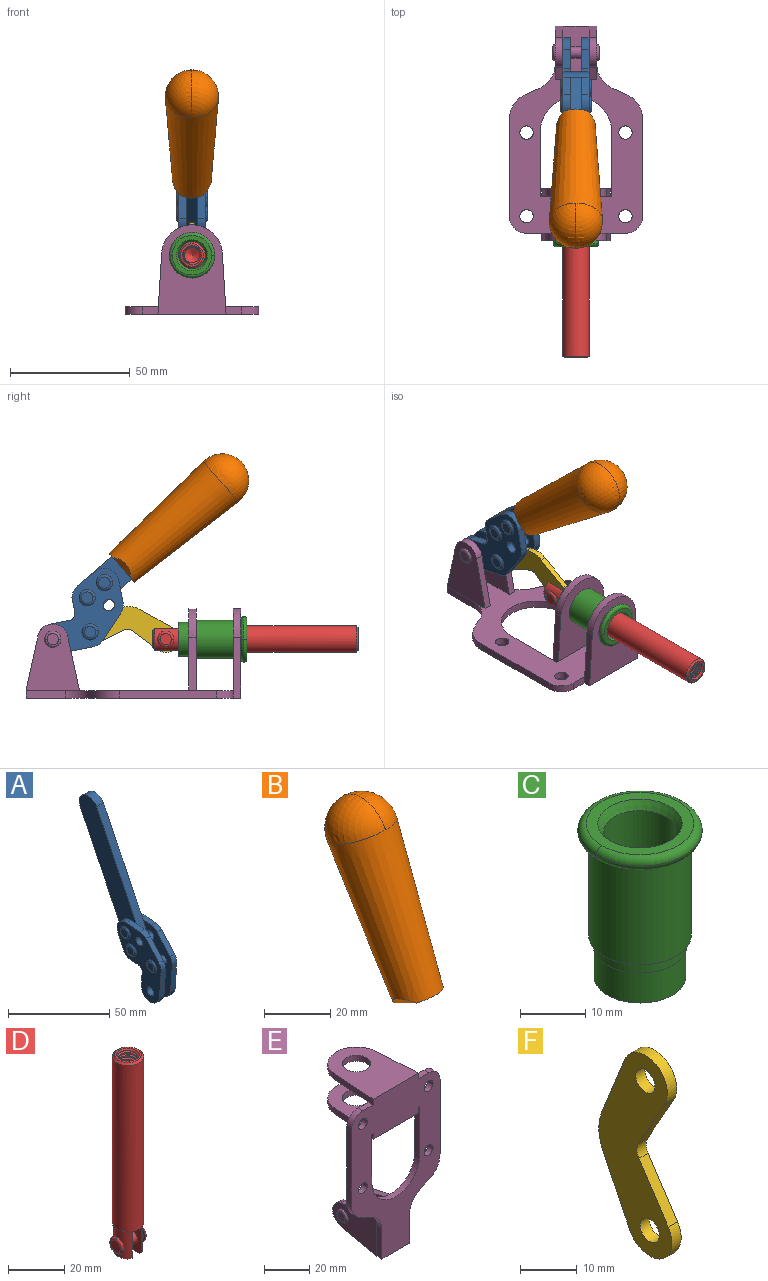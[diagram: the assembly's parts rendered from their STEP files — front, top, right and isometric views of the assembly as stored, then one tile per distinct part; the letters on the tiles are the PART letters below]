
ASSEMBLY  parts=6 mates=7
PART A: 59 faces, bbox 12.9x60.2x99.6 mm
  f0: torus R=2.39mm, axis (-1,0,0), area 14.9mm2, adj f20,f43,f51
  f1: torus R=2.39mm, axis (-1,0,0), area 14.9mm2, adj f19,f42,f51
  f2: torus R=2.39mm, axis (-1,0,0), area 14.9mm2, adj f18,f35,f51
  f3: torus R=2.39mm, axis (-1,0,0), area 14.9mm2, adj f14,f17,f23
  f4: torus R=2.39mm, axis (-1,0,0), area 14.9mm2, adj f13,f16,f23
  f5: torus R=2.39mm, axis (-1,0,0), area 14.9mm2, adj f12,f15,f23
  f6: cylinder r=2.39mm len=4.78mm, axis (1,0,0), area 46.5mm2, adj f48,f50,f51
  f7: cylinder r=2.39mm len=4.78mm, axis (1,0,0), area 46.5mm2, adj f50,f51
  f8: cylinder r=6.35mm len=12.68mm, axis (1,0,0), area 61.8mm2, adj f38,f39,f50,f51
  f9: cylinder r=2.39mm len=4.78mm, axis (-1,0,0), area 70.5mm2, adj f46,f50
  f10: cylinder r=2.39mm len=4.78mm, axis (-1,0,0), area 46.5mm2, adj f23,f45,f46
  f11: cylinder r=2.39mm len=4.78mm, axis (-1,0,0), area 46.5mm2, adj f23,f46
  f12: plane 4.78x4.78mm, normal (1,0,0), area 17.9mm2, adj f5,f15
  f13: plane 4.78x4.78mm, normal (1,0,0), area 17.9mm2, adj f4,f16
  f14: plane 4.78x4.78mm, normal (1,0,0), area 17.9mm2, adj f3,f17
  f15: torus R=2.39mm, axis (-1,0,0), area 14.9mm2, adj f5,f12,f23
  f16: torus R=2.39mm, axis (-1,0,0), area 14.9mm2, adj f4,f13,f23
  f17: torus R=2.39mm, axis (-1,0,0), area 14.9mm2, adj f3,f14,f23
  f18: plane 4.78x4.78mm, normal (-1,0,0), area 17.9mm2, adj f2,f35
  f19: plane 4.78x4.78mm, normal (-1,0,0), area 17.9mm2, adj f1,f42
  f20: plane 4.78x4.78mm, normal (-1,0,0), area 17.9mm2, adj f0,f43
  f21: plane 2.26x0.2mm, normal (1,0,0), area 0.2mm2, adj f31,f44
  f22: plane 2.26x0.2mm, normal (-1,0,0), area 0.2mm2, adj f41,f44
  f23: plane 39.37x30.77mm, normal (1,0,0), area 565.5mm2, adj f3,f4,f5,f10,f11,f15,f16,f17
  f24: cylinder r=6.1mm len=4.15mm, axis (-1,0,0), area 14.7mm2, adj f23,f25,f32,f46
  f25: plane 10.25x9.01mm, normal (0,-0.75,0.66), area 42.3mm2, adj f23,f24,f26,f46
  f26: cylinder r=6.35mm len=4.64mm, axis (-1,0,0), area 15.6mm2, adj f23,f25,f27,f46
  f27: plane 15.84x3.1mm, normal (0,-1,-0.07), area 49.2mm2, adj f23,f26,f28,f46
  f28: cylinder r=6.35mm len=12.68mm, axis (-1,0,0), area 61.8mm2, adj f23,f27,f29,f46
  f29: plane 8.11x3.1mm, normal (0,1,0.07), area 25.2mm2, adj f23,f28,f30,f46
  f30: cylinder r=3.05mm len=3.25mm, axis (-1,0,0), area 14.8mm2, adj f23,f29,f31,f46
  f31: plane 5.99x3.1mm, normal (0,0.07,-1), area 18.6mm2, adj f21,f23,f30,f44,f46
  f32: plane 9.5x3.1mm, normal (0,-0.07,1), area 29.5mm2, adj f23,f24,f33,f46,f47
  f33: cylinder r=6.1mm len=8.63mm, axis (-1,0,0), area 39.1mm2, adj f23,f32,f34,f47
  f34: plane 8.65x3.96mm, normal (0,0.91,-0.42), area 29.5mm2, adj f23,f33,f44,f47
  f35: torus R=2.39mm, axis (-1,0,0), area 14.9mm2, adj f2,f18,f51
  f36: plane 10.25x9.01mm, normal (0,-0.75,0.66), area 42.3mm2, adj f37,f49,f50,f51
  f37: cylinder r=6.35mm len=4.64mm, axis (1,0,0), area 15.6mm2, adj f36,f38,f50,f51
  f38: plane 15.84x3.1mm, normal (0,-1,-0.07), area 49.2mm2, adj f8,f37,f50,f51
  f39: plane 8.11x3.1mm, normal (0,1,0.07), area 25.2mm2, adj f8,f40,f50,f51
  f40: cylinder r=3.05mm len=3.25mm, axis (1,0,0), area 14.8mm2, adj f39,f41,f50,f51
  f41: plane 5.99x3.1mm, normal (0,0.07,-1), area 18.6mm2, adj f22,f40,f44,f50,f51
  f42: torus R=2.39mm, axis (-1,0,0), area 14.9mm2, adj f1,f19,f51
  f43: torus R=2.39mm, axis (-1,0,0), area 14.9mm2, adj f0,f20,f51
  f44: cylinder r=6.35mm len=12.12mm, axis (-1,0,0), area 128.9mm2, adj f21,f22,f23,f31,f34,f41,f46,f47
  f45: plane 2.65x1.35mm, normal (1,0,0), area 1mm2, adj f10,f55
  f46: plane 39.08x20.42mm, normal (-1,0,0), area 412.5mm2, adj f9,f10,f11,f24,f25,f26,f27,f28
  f47: plane 77.62x39.82mm, normal (1,0,0), area 850mm2, adj f32,f33,f34,f44,f53,f54,f55
  f48: plane 2.65x1.35mm, normal (-1,0,0), area 1mm2, adj f6,f55
  f49: cylinder r=6.1mm len=4.15mm, axis (1,0,0), area 14.7mm2, adj f36,f50,f51,f56
  f50: plane 39.08x20.42mm, normal (1,0,0), area 412.5mm2, adj f6,f7,f8,f9,f36,f37,f38,f39
  f51: plane 39.37x30.77mm, normal (-1,0,0), area 565.5mm2, adj f0,f1,f2,f6,f7,f8,f35,f36
  f52: plane 8.65x3.96mm, normal (0,0.91,-0.42), area 29.5mm2, adj f44,f51,f57,f58
  f53: plane 68.49x33.4mm, normal (0,0.9,-0.44), area 358.1mm2, adj f44,f47,f54,f58
  f54: cylinder r=6.35mm len=12.06mm, axis (1,0,0), area 93.7mm2, adj f47,f53,f55,f58
  f55: plane 68.49x33.4mm, normal (0,-0.9,0.44), area 358.1mm2, adj f44,f45,f46,f47,f48,f50,f54,f58
  f56: plane 9.5x3.1mm, normal (0,-0.07,1), area 29.5mm2, adj f49,f50,f51,f57,f58
  f57: cylinder r=6.1mm len=8.63mm, axis (1,0,0), area 39.1mm2, adj f51,f52,f56,f58
  f58: plane 77.62x39.82mm, normal (-1,0,0), area 850mm2, adj f44,f52,f53,f54,f55,f56,f57
PART B: 11 faces, bbox 22.3x42.6x64.5 mm
  f0: sphere r=11.13mm, area 411.4mm2, adj f1,f8
  f1: cone r=11.11mm half-angle=3.3deg, axis (0,0.44,0.9), area 3251.8mm2, adj f0,f7,f8,f9,f10
  f2: cylinder r=6.16mm len=11.7mm, axis (1,0,0), area 89.5mm2, adj f3,f4,f5,f6
  f3: plane 60.23x36.75mm, normal (-1,0,0), area 763.6mm2, adj f2,f4,f6,f10
  f4: plane 51.37x25.05mm, normal (0,0.9,-0.44), area 264.2mm2, adj f2,f3,f5,f10
  f5: plane 60.23x36.75mm, normal (1,0,0), area 763.6mm2, adj f2,f4,f6,f10
  f6: plane 51.37x25.05mm, normal (0,-0.9,0.44), area 264.2mm2, adj f2,f3,f5,f10
  f7: plane 9.95x5.95mm, normal (0.71,-0.31,-0.64), area 25.8mm2, adj f1,f10
  f8: sphere r=11.13mm, area 411.4mm2, adj f0,f1
  f9: plane 9.95x5.95mm, normal (-0.71,-0.31,-0.64), area 25.8mm2, adj f1,f10
  f10: plane 14.27x11.38mm, normal (0,-0.44,-0.9), area 106.7mm2, adj f1,f3,f4,f5,f6,f7,f9
PART C: 15 faces, bbox 20.6x20.6x28.7 mm
  f0: torus R=8.26mm, axis (0,0,1), area 56.8mm2, adj f1,f10,f12
  f1: torus R=8.26mm, axis (0,0,1), area 56.8mm2, adj f0,f6,f13
  f2: cylinder r=5.59mm len=25.91mm, axis (0,0,1), area 909.6mm2, adj f3,f4
  f3: cone r=6.86mm half-angle=45deg, axis (0,0,-1), area 70.2mm2, adj f2,f14
  f4: cone r=6.47mm half-angle=30deg, axis (0,0,1), area 66.7mm2, adj f2,f13
  f5: cylinder r=7.04mm len=14.07mm, axis (0,0,1), area 252.6mm2, adj f11,f14
  f6: torus R=8.26mm, axis (0,0,1), area 56.8mm2, adj f1,f12,f13
  f7: cylinder r=7.16mm len=14.33mm, axis (0,0,1), area 91.5mm2, adj f9,f11
  f8: cylinder r=7.86mm len=18.42mm, axis (0,0,1), area 909.6mm2, adj f9,f10
  f9: plane 15.72x15.72mm, normal (0,0,-1), area 33mm2, adj f7,f8
  f10: plane 16.51x16.51mm, normal (0,0,-1), area 19.9mm2, adj f0,f8,f12
  f11: plane 14.33x14.33mm, normal (0,0,-1), area 5.7mm2, adj f5,f7
  f12: torus R=8.26mm, axis (0,0,1), area 56.8mm2, adj f0,f6,f10
  f13: plane 16.51x16.51mm, normal (0,0,1), area 82.7mm2, adj f1,f4,f6
  f14: plane 14.07x14.07mm, normal (0,0,-1), area 7.8mm2, adj f3,f5
PART D: 48 faces, bbox 12.6x11.1x86.1 mm
  f0: torus R=2.41mm, axis (-1,0,0), area 15mm2, adj f30,f32,f34
  f1: torus R=2.41mm, axis (-1,0,0), area 15mm2, adj f29,f31,f33
  f2: cylinder r=5.54mm len=72.39mm, axis (0,0,1), area 2518.5mm2, adj f3,f4,f42,f43
  f3: cone r=5.54mm half-angle=45deg, axis (0,0,1), area 7.6mm2, adj f2,f5,f41
  f4: cone r=5.54mm half-angle=45deg, axis (0,0,-1), area 34.9mm2, adj f2,f39
  f5: cylinder r=5.08mm len=11.48mm, axis (0,0,1), area 108.3mm2, adj f3,f7,f8,f41
  f6: cylinder r=2.41mm len=4.83mm, axis (-1,0,0), area 71.2mm2, adj f40,f41
  f7: cylinder r=2.41mm len=4.83mm, axis (-1,0,0), area 7.6mm2, adj f5,f34
  f8: cone r=5.08mm half-angle=45deg, axis (0,0,1), area 10.6mm2, adj f5,f37,f41
  f9: cone r=3.98mm half-angle=45deg, axis (0,0,1), area 17.6mm2, adj f27,f39,f45,f46,f47
  f10: cylinder r=2.41mm len=4.83mm, axis (-1,0,0), area 7.6mm2, adj f33,f38
  f11: cylinder r=3.2mm len=6.4mm, axis (0,0,1), area 78.4mm2, adj f12,f28,f44,f45,f47
  f12: cylinder r=3.2mm len=6.4mm, axis (0,0,1), area 10.5mm2, adj f11,f13,f45,f47
  f13: cylinder r=3.2mm len=6.4mm, axis (0,0,1), area 10.5mm2, adj f12,f14,f45,f47
  f14: cylinder r=3.2mm len=6.4mm, axis (0,0,1), area 10.5mm2, adj f13,f15,f45,f47
  f15: cylinder r=3.2mm len=6.4mm, axis (0,0,1), area 10.5mm2, adj f14,f16,f45,f47
  f16: cylinder r=3.2mm len=6.4mm, axis (0,0,1), area 10.5mm2, adj f15,f17,f45,f47
  f17: cylinder r=3.2mm len=6.4mm, axis (0,0,1), area 10.5mm2, adj f16,f18,f45,f47
  f18: cylinder r=3.2mm len=6.4mm, axis (0,0,1), area 10.5mm2, adj f17,f19,f45,f47
  f19: cylinder r=3.2mm len=6.4mm, axis (0,0,1), area 10.5mm2, adj f18,f20,f45,f47
  f20: cylinder r=3.2mm len=6.4mm, axis (0,0,1), area 10.5mm2, adj f19,f21,f45,f47
  f21: cylinder r=3.2mm len=6.4mm, axis (0,0,1), area 10.5mm2, adj f20,f22,f45,f47
  f22: cylinder r=3.2mm len=6.4mm, axis (0,0,1), area 10.5mm2, adj f21,f23,f45,f47
  f23: cylinder r=3.2mm len=6.4mm, axis (0,0,1), area 10.5mm2, adj f22,f24,f45,f47
  f24: cylinder r=3.2mm len=6.4mm, axis (0,0,1), area 10.5mm2, adj f23,f25,f45,f47
  f25: cylinder r=3.2mm len=6.4mm, axis (0,0,1), area 10.5mm2, adj f24,f26,f45,f47
  f26: cylinder r=3.2mm len=6.4mm, axis (0,0,1), area 10.5mm2, adj f25,f27,f45,f47
  f27: cylinder r=3.2mm len=6.4mm, axis (0,0,1), area 7.4mm2, adj f9,f26,f45,f47
  f28: cone r=3.2mm half-angle=60deg, axis (0,0,1), area 37.2mm2, adj f11
  f29: plane 4.83x4.83mm, normal (-1,0,0), area 18.3mm2, adj f1,f31
  f30: plane 4.83x4.83mm, normal (1,0,0), area 18.3mm2, adj f0,f32
  f31: torus R=2.41mm, axis (-1,0,0), area 15mm2, adj f1,f29,f33
  f32: torus R=2.41mm, axis (-1,0,0), area 15mm2, adj f0,f30,f34
  f33: plane 6.83x6.83mm, normal (1,0,0), area 18.3mm2, adj f1,f10,f31
  f34: plane 6.83x6.83mm, normal (-1,0,0), area 18.3mm2, adj f0,f7,f32
  f35: cone r=5.08mm half-angle=45deg, axis (0,0,1), area 10.6mm2, adj f36,f38,f40
  f36: plane 7.25x1.97mm, normal (0,0,-1), area 10mm2, adj f35,f40
  f37: plane 7.25x1.97mm, normal (0,0,-1), area 10mm2, adj f8,f41
  f38: cylinder r=5.08mm len=11.48mm, axis (0,0,1), area 108.3mm2, adj f10,f35,f40,f42
  f39: plane 9.55x9.55mm, normal (0,0,1), area 22mm2, adj f4,f9
  f40: plane 12.76x10.09mm, normal (1,0,0), area 95.7mm2, adj f6,f35,f36,f38,f42,f43
  f41: plane 12.76x10.09mm, normal (-1,0,0), area 95.7mm2, adj f3,f5,f6,f8,f37,f43
  f42: cone r=5.54mm half-angle=45deg, axis (0,0,1), area 7.6mm2, adj f2,f38,f40
  f43: plane 11.07x4.7mm, normal (0,0,-1), area 50.4mm2, adj f2,f40,f41
  f44: plane 0.89x0.62mm, normal (-1,0,0), area 0.3mm2, adj f11,f45,f46,f47
  f45: bspline ~24.8x7.63mm, area 266.6mm2, adj f9,f11,f12,f13,f14,f15,f16,f17
  f46: bspline ~24.87x7.63mm, area 73.6mm2, adj f9,f44,f45,f47
  f47: bspline ~24.98x7.63mm, area 272.5mm2, adj f9,f11,f12,f13,f14,f15,f16,f17
PART E: 55 faces, bbox 55.7x37.4x89.8 mm
  f0: torus R=2.41mm, axis (-1,0,0), area 15mm2, adj f11,f15,f25
  f1: torus R=2.41mm, axis (-1,0,0), area 15mm2, adj f10,f12,f22
  f2: cylinder r=2.78mm len=5.56mm, axis (0,-1,0), area 54.2mm2, adj f30,f54
  f3: cylinder r=14.99mm len=29.97mm, axis (0,-1,0), area 145.9mm2, adj f30,f49,f53,f54
  f4: cylinder r=2.78mm len=5.56mm, axis (0,-1,0), area 54.2mm2, adj f30,f54
  f5: cylinder r=2.78mm len=5.56mm, axis (0,-1,0), area 54.2mm2, adj f30,f54
  f6: cylinder r=2.78mm len=5.56mm, axis (0,-1,0), area 54.2mm2, adj f30,f54
  f7: cylinder r=6.35mm len=12.7mm, axis (0,0,1), area 123.6mm2, adj f27,f51
  f8: cylinder r=6.35mm len=12.7mm, axis (0,0,-1), area 124.7mm2, adj f21,f35
  f9: cylinder r=2.41mm len=11.18mm, axis (-1,0,0), area 169.4mm2, adj f16,f19
  f10: plane 4.83x4.83mm, normal (1,0,0), area 18.3mm2, adj f1,f12
  f11: plane 4.83x4.83mm, normal (-1,0,0), area 18.3mm2, adj f0,f15
  f12: torus R=2.41mm, axis (-1,0,0), area 15mm2, adj f1,f10,f22
  f13: cylinder r=6.35mm len=12.41mm, axis (1,0,0), area 53.4mm2, adj f18,f19,f22,f23
  f14: cylinder r=6.35mm len=12.41mm, axis (-1,0,0), area 53.4mm2, adj f16,f17,f24,f25
  f15: torus R=2.41mm, axis (-1,0,0), area 15mm2, adj f0,f11,f25
  f16: plane 27.86x22.35mm, normal (1,0,0), area 425.4mm2, adj f9,f14,f17,f24,f30
  f17: plane 22.86x4.97mm, normal (0,0.21,0.98), area 72.5mm2, adj f14,f16,f25,f30
  f18: plane 22.86x4.97mm, normal (0,0.21,0.98), area 72.5mm2, adj f13,f19,f22,f30
  f19: plane 27.86x22.35mm, normal (-1,0,0), area 425.4mm2, adj f9,f13,f18,f23,f30
  f20: cylinder r=12.7mm len=25.35mm, axis (0,0,-1), area 119.8mm2, adj f21,f34,f35,f36
  f21: plane 34.21x28.07mm, normal (0,0,-1), area 702.4mm2, adj f8,f20,f30,f34,f36
  f22: plane 27.96x22.45mm, normal (1,0,0), area 407.2mm2, adj f1,f12,f13,f18,f23,f30,f42,f43
  f23: plane 22.86x4.97mm, normal (0,0.21,-0.98), area 72.5mm2, adj f13,f19,f22,f44
  f24: plane 22.86x4.97mm, normal (0,0.21,-0.98), area 72.5mm2, adj f14,f16,f25,f44
  f25: plane 27.86x22.35mm, normal (-1,0,0), area 407.1mm2, adj f0,f14,f15,f17,f24,f30,f45,f46
  f26: plane 3.1x0.95mm, normal (0,0,-1), area 2.7mm2, adj f30,f49,f50,f54
  f27: plane 34.21x28.07mm, normal (0,0,1), area 702.4mm2, adj f7,f28,f30,f50,f52
  f28: cylinder r=12.7mm len=25.35mm, axis (0,0,1), area 118.8mm2, adj f27,f50,f51,f52
  f29: plane 3.1x0.95mm, normal (0,0,-1), area 2.7mm2, adj f30,f52,f53,f54
  f30: plane 86.54x55.63mm, normal (0,1,0), area 2362.9mm2, adj f2,f3,f4,f5,f6,f16,f17,f18
  f31: plane 40.56x3.1mm, normal (-1,0,0), area 125.7mm2, adj f30,f32,f48,f54
  f32: cylinder r=7.11mm len=7.11mm, axis (0,-1,0), area 34.6mm2, adj f30,f31,f33,f54
  f33: plane 6.67x3.1mm, normal (0,0,1), area 20.4mm2, adj f30,f32,f34,f54
  f34: plane 25.39x3.13mm, normal (-1,0.06,0), area 79.5mm2, adj f20,f21,f33,f35,f54
  f35: plane 37.31x28.45mm, normal (0,0,1), area 789.9mm2, adj f8,f20,f34,f36,f54
  f36: plane 25.39x3.13mm, normal (1,0.06,0), area 79.5mm2, adj f20,f21,f35,f37,f54
  f37: plane 6.67x3.1mm, normal (0,0,1), area 20.4mm2, adj f30,f36,f38,f54
  f38: cylinder r=7.11mm len=7.11mm, axis (0,-1,0), area 34.6mm2, adj f30,f37,f39,f54
  f39: plane 40.56x3.1mm, normal (1,0,0), area 125.7mm2, adj f30,f38,f40,f54
  f40: cylinder r=11.18mm len=10.16mm, axis (0,-1,0), area 39.5mm2, adj f30,f39,f41,f54
  f41: plane 6.09x3.1mm, normal (0.42,0,-0.91), area 20.8mm2, adj f30,f40,f42,f54
  f42: cylinder r=11.18mm len=9.41mm, axis (0,-1,0), area 37.2mm2, adj f22,f30,f41,f43,f54
  f43: plane 16.5x3.1mm, normal (1,0,0), area 51.1mm2, adj f22,f42,f44,f54
  f44: plane 17.37x3.1mm, normal (0,0,-1), area 53.8mm2, adj f23,f24,f30,f43,f45,f54
  f45: plane 16.5x3.1mm, normal (-1,0,0), area 51.1mm2, adj f25,f44,f46,f54
  f46: cylinder r=11.18mm len=9.41mm, axis (0,-1,0), area 37.2mm2, adj f25,f30,f45,f47,f54
  f47: plane 6.09x3.1mm, normal (-0.42,0,-0.91), area 20.8mm2, adj f30,f46,f48,f54
  f48: cylinder r=11.18mm len=10.16mm, axis (0,-1,0), area 39.5mm2, adj f30,f31,f47,f54
  f49: plane 26.54x3.1mm, normal (-1,0,0), area 82.3mm2, adj f3,f26,f30,f54
  f50: plane 25.39x3.1mm, normal (1,0.06,0), area 78.8mm2, adj f26,f27,f28,f51,f54
  f51: plane 37.31x28.45mm, normal (0,0,-1), area 789.9mm2, adj f7,f28,f50,f52,f54
  f52: plane 25.39x3.1mm, normal (-1,0.06,0), area 78.8mm2, adj f27,f28,f29,f51,f54
  f53: plane 26.54x3.1mm, normal (1,0,0), area 82.3mm2, adj f3,f29,f30,f54
  f54: plane 89.66x55.63mm, normal (0,-1,0), area 2678.5mm2, adj f2,f3,f4,f5,f6,f26,f29,f31
PART F: 12 faces, bbox 2.3x18.2x42.8 mm
  f0: cylinder r=2.4mm len=4.8mm, axis (1,0,0), area 34.9mm2, adj f4,f11
  f1: cylinder r=10.41mm len=8.47mm, axis (1,0,0), area 20.2mm2, adj f4,f9,f10,f11
  f2: cylinder r=3.05mm len=3.16mm, axis (1,0,0), area 7.7mm2, adj f4,f6,f7,f11
  f3: cylinder r=2.4mm len=4.8mm, axis (1,0,0), area 34.9mm2, adj f4,f11
  f4: plane 42.81x18.23mm, normal (-1,0,0), area 414.1mm2, adj f0,f1,f2,f3,f5,f6,f7,f8
  f5: cylinder r=5.54mm len=10.67mm, axis (1,0,0), area 41.8mm2, adj f4,f6,f10,f11
  f6: plane 11.66x6.53mm, normal (0,-0.87,-0.49), area 30.9mm2, adj f2,f4,f5,f11
  f7: plane 11.17x7.33mm, normal (0,-0.84,0.55), area 30.9mm2, adj f2,f4,f8,f11
  f8: cylinder r=5.54mm len=10.51mm, axis (1,0,0), area 41.8mm2, adj f4,f7,f9,f11
  f9: plane 13.67x6.67mm, normal (0,0.9,-0.44), area 35.1mm2, adj f1,f4,f8,f11
  f10: plane 14.1x5.7mm, normal (0,0.93,0.37), area 35.1mm2, adj f1,f4,f5,f11
  f11: plane 42.81x18.23mm, normal (1,0,0), area 414.1mm2, adj f0,f1,f2,f3,f5,f6,f7,f8
PLACE A rot(axis=(1,0,0),75deg) t=(0,3.86,9.14)mm
PLACE B rot(axis=(1,0,0),75deg) t=(-0.04,3.86,9.14)mm
PLACE C rot(axis=(1,0,0),90deg) t=(0,9.14,0)mm
PLACE D rot(axis=(1,0,0),90deg) t=(0,9.52,0)mm
PLACE E rot(axis=(1,0,0),90deg) t=(0,9.14,0)mm
PLACE F rot(axis=(1,0,0),97.5deg) t=(0,12.59,2.22)mm
MATE revolute F.f5 <-> D.f6  axis (1,0,0) through (0,-5.96,24.61)mm
MATE slider D.f2 <-> C.f12  axis (0,-1,0) through (0,-49.26,24.61)mm
MATE fastened C.f2 <-> E.f7  axis (0,1,0) through (0,-37.25,24.61)mm
MATE fastened B.f2 <-> A.f54  axis (1,0,0) through (-2.35,-30.66,91.94)mm
MATE revolute F.f3 <-> A.f4  axis (1,0,0) through (0,25.65,27.64)mm
MATE revolute A.f7 <-> E.f0  axis (1,0,0) through (0,41.23,24.61)mm
MATE slider D.f2 <-> E.f7  axis (0,-1,0) through (0,-49.26,24.61)mm
